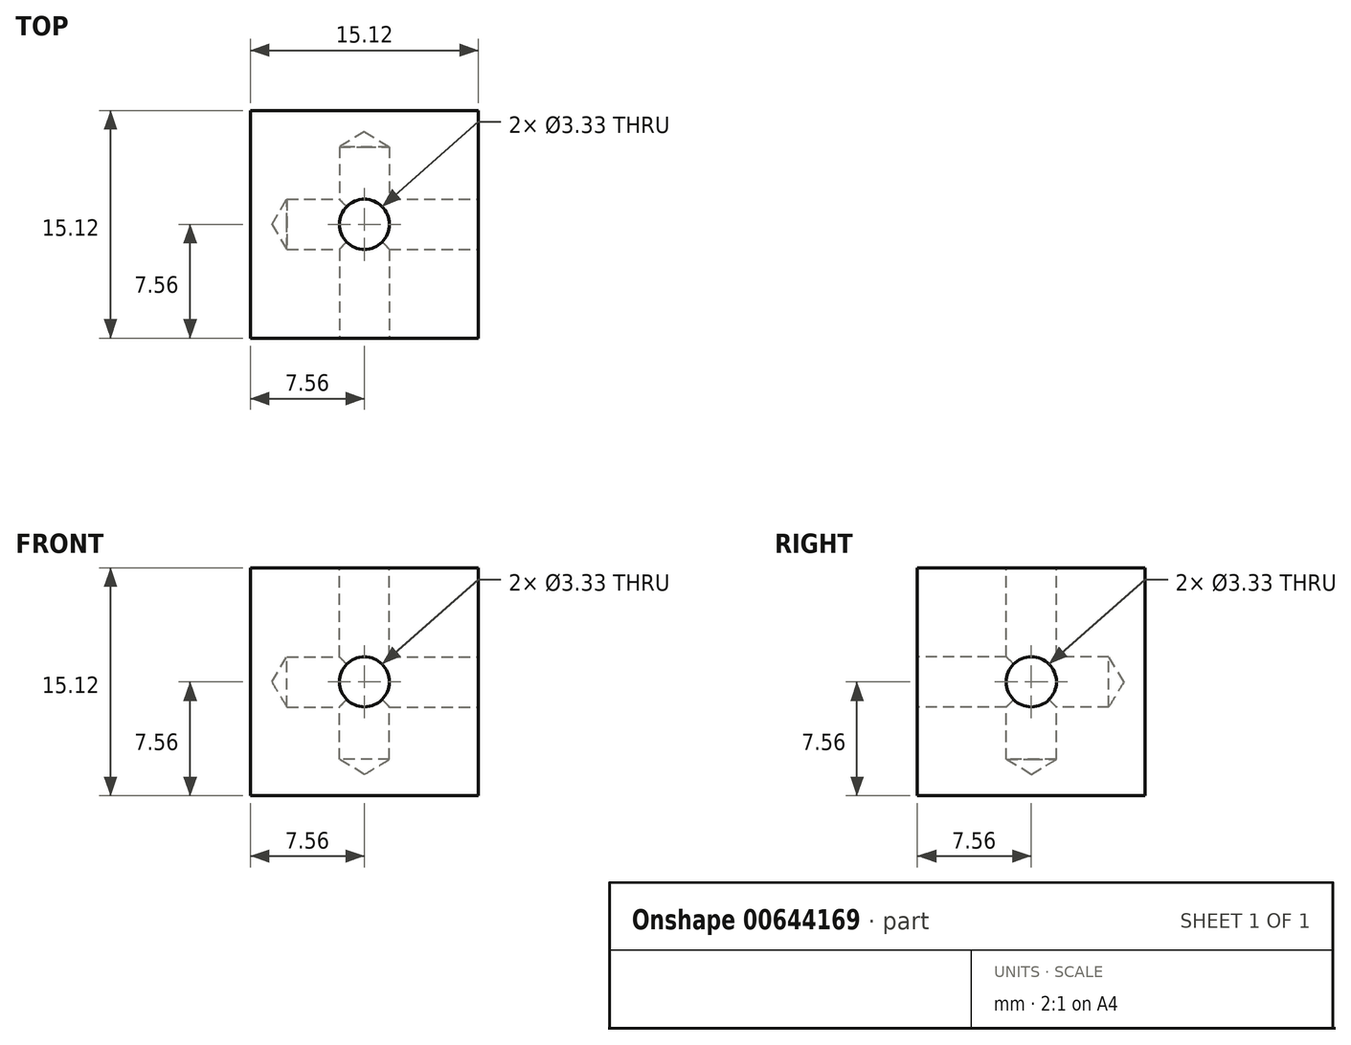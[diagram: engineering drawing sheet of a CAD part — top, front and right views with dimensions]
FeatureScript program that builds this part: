
annotation { "Feature Type Name" : "Feature", "Feature Type Description" : "" }
export const myFeature = defineFeature(function(context is Context, id is Id, definition is map)
    precondition{}
    {
        {
            var Q0;
            Q0=qCreatedBy(makeId("Front.planeOp"),FACE);
            var sketch = newSketch(context, id + "F0", { "sketchPlane" : qUnion([Q0])});
            skLineSegment(sketch, "E0.bottom", {"start": v(7.56, 7.56) * mm, "end": v(-7.56, 7.56) * mm});
            skLineSegment(sketch, "E0.top", {"start": v(7.56, -7.56) * mm, "end": v(-7.56, -7.56) * mm});
            skLineSegment(sketch, "E0.left", {"start": v(7.56, 7.56) * mm, "end": v(7.56, -7.56) * mm});
            skLineSegment(sketch, "E0.right", {"start": v(-7.56, 7.56) * mm, "end": v(-7.56, -7.56) * mm});
            skPoint(sketch, "E0.middle", {"position": v(0, 0) * mm});
            skSolve(sketch);
        }
        {
            var Q0;
            Q0 = qSketchRegion(id + "F0", true);
            extrude(context, id + "F1", {"entities" : qUnion([Q0]), "endBound" : BoundingType.SYMMETRIC, "depth" : 15.1 * mm, "offsetDistance" : 25.4 * mm});
        }
        {
            var Q0;
            Q0=makeQuery(id+"F1.opExtrude","CAP_FACE",FACE,{"disambiguationData":[OSD([sQuery(id+"F0.wireOp",EDGE,"E0.bottom"),sQuery(id+"F0.wireOp",EDGE,"E0.top"),sQuery(id+"F0.wireOp",EDGE,"E0.left"),sQuery(id+"F0.wireOp",EDGE,"E0.right")])],"isStart":false});
            var sketch = newSketch(context, id + "F2", { "sketchPlane" : qUnion([Q0])});
            skPoint(sketch, "E1", {"position": v(0, 0) * mm});
            skSolve(sketch);
        }
        {
            var Q0;
            Q0=sQuery(id+"F2.wireOp",VERTEX,"E1");
            var Q1;
            Q1=makeQuery(id+"F1.opExtrude","SWEPT_BODY",BODY,{"disambiguationData":[OSD([sQuery(id+"F0.wireOp",EDGE,"E0.bottom"),sQuery(id+"F0.wireOp",EDGE,"E0.top"),sQuery(id+"F0.wireOp",EDGE,"E0.left"),sQuery(id+"F0.wireOp",EDGE,"E0.right")])]});
            hole(context, id + "F3", {"style" : HoleStyle.SIMPLE, "endStyle" : HoleEndStyle.BLIND, "holeDiameter" : 3.33 * mm, "majorDiameter" : 6.35 * mm, "holeDepth" : 12.7 * mm, "isTappedThrough" : true, "tappedDepth" : 12.7 * mm, "tapClearance" : 3, "locations" : qUnion([Q0]), "scope" : qUnion([Q1])});
        }
        {
            var Q0;
            Q0=makeQuery(id+"F1.opExtrude","SWEPT_FACE",FACE,{"disambiguationData":[OSD([sQuery(id+"F0.wireOp",EDGE,"E0.bottom")])]});
            var sketch = newSketch(context, id + "F4", { "sketchPlane" : qUnion([Q0])});
            skPoint(sketch, "E2", {"position": v(0, 0) * mm});
            skSolve(sketch);
        }
        {
            var Q0;
            Q0=sQuery(id+"F4.wireOp",VERTEX,"E2");
            var Q1;
            Q1=makeQuery(id+"F1.opExtrude","SWEPT_BODY",BODY,{"disambiguationData":[OSD([sQuery(id+"F0.wireOp",EDGE,"E0.bottom"),sQuery(id+"F0.wireOp",EDGE,"E0.top"),sQuery(id+"F0.wireOp",EDGE,"E0.left"),sQuery(id+"F0.wireOp",EDGE,"E0.right")])]});
            hole(context, id + "F5", {"style" : HoleStyle.SIMPLE, "endStyle" : HoleEndStyle.BLIND, "holeDiameter" : 3.33 * mm, "majorDiameter" : 6.35 * mm, "holeDepth" : 12.7 * mm, "isTappedThrough" : true, "tappedDepth" : 12.7 * mm, "tapClearance" : 3, "locations" : qUnion([Q0]), "scope" : qUnion([Q1])});
        }
        {
            var Q0;
            Q0=makeQuery(id+"F1.opExtrude","SWEPT_FACE",FACE,{"disambiguationData":[OSD([sQuery(id+"F0.wireOp",EDGE,"E0.left")])]});
            var sketch = newSketch(context, id + "F6", { "sketchPlane" : qUnion([Q0])});
            skPoint(sketch, "E3", {"position": v(0, 0) * mm});
            skSolve(sketch);
        }
        {
            var Q0;
            Q0=sQuery(id+"F6.wireOp",VERTEX,"E3");
            var Q1;
            Q1=makeQuery(id+"F1.opExtrude","SWEPT_BODY",BODY,{"disambiguationData":[OSD([sQuery(id+"F0.wireOp",EDGE,"E0.bottom"),sQuery(id+"F0.wireOp",EDGE,"E0.top"),sQuery(id+"F0.wireOp",EDGE,"E0.left"),sQuery(id+"F0.wireOp",EDGE,"E0.right")])]});
            hole(context, id + "F7", {"style" : HoleStyle.SIMPLE, "endStyle" : HoleEndStyle.BLIND, "holeDiameter" : 3.33 * mm, "majorDiameter" : 6.35 * mm, "holeDepth" : 12.7 * mm, "isTappedThrough" : true, "tappedDepth" : 12.7 * mm, "tapClearance" : 3, "locations" : qUnion([Q0]), "scope" : qUnion([Q1])});
        }
    });
